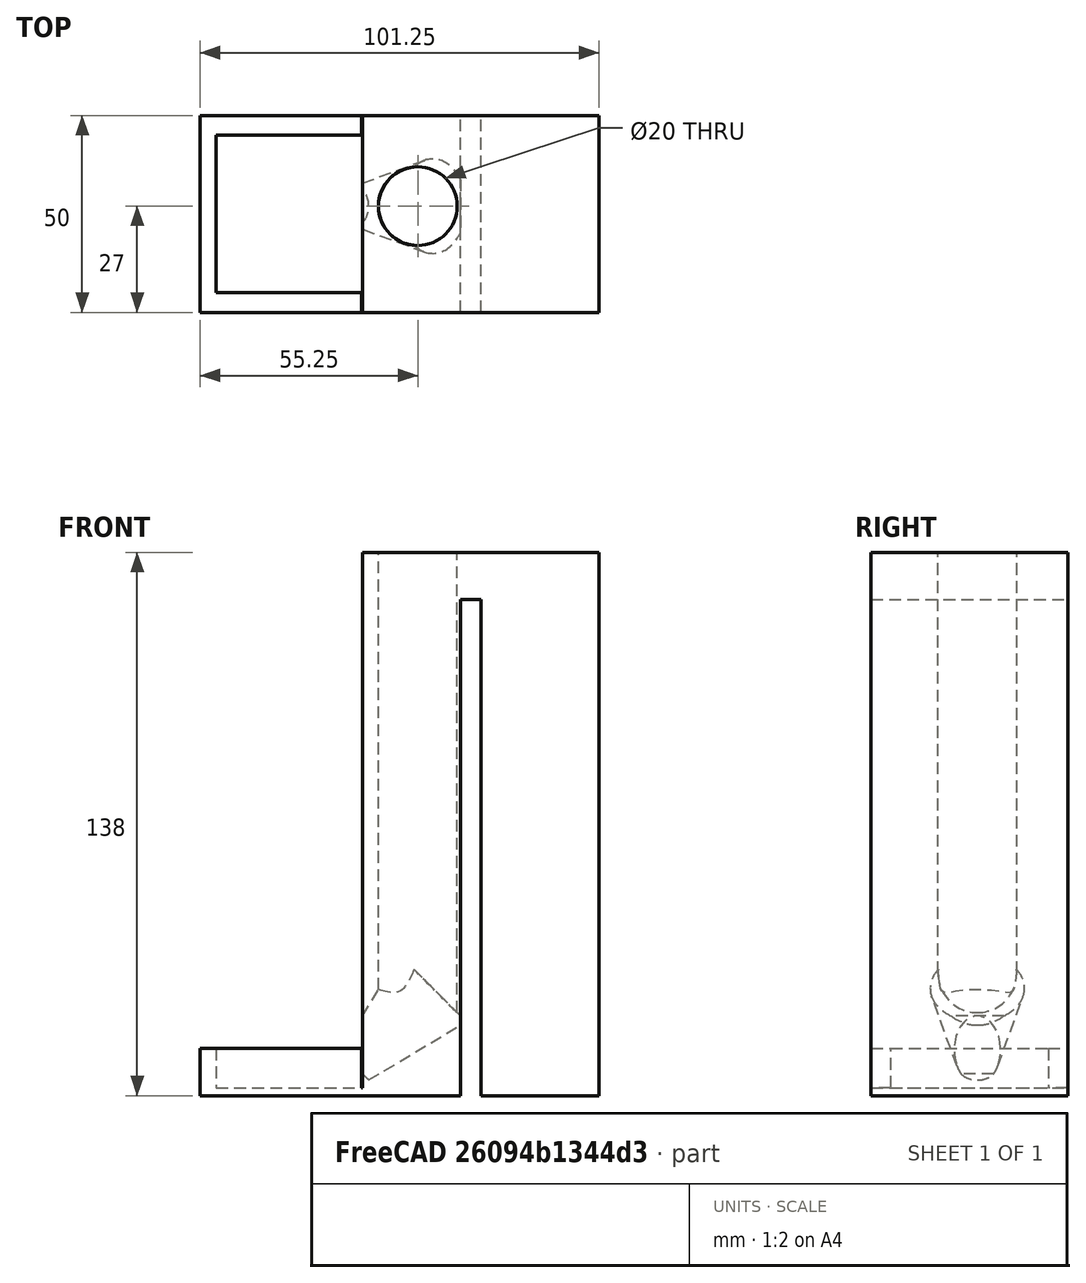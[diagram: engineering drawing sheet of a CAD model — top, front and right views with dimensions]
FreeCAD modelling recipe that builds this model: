
FCSTD DOCUMENT  (FreeCAD 0.17R13522 (Git))
Label: new reward no top
License: All rights reserved
LicenseURL: http://en.wikipedia.org/wiki/All_rights_reserved
objects: Part::Box×6, Part::Fuse×4, Part::Cut×3, Part::Cylinder×1, Part::Cone×1
note: 15 computed .brp shape members not serialized (recipe doc carries the construction recipe); baked Part::Feature solids carry a one-line shape summary decoded from their .brp

FEATURE [Part::Box] Box001  label="Cube001"
  AttacherType = Attacher::AttachEngine3D
  Height = 138
  Length = 60
  Placement = pos=(-30,32,-10) rot=(0,0,1;0rad)
  Width = 50
FEATURE [Part::Box] Box002  label="Cube002"
  AttacherType = Attacher::AttachEngine3D
  Height = 126
  Length = 5.2
  Placement = pos=(-5.2,32,-10) rot=(0,0,1;0rad)
  Width = 50
FEATURE [Part::Cylinder] Cylinder
  Angle = 360
  AttacherType = Attacher::AttachEngine3D
  Height = 129
  Placement = pos=(-16,59,11) rot=(0,0,1;0rad)
  Radius = 10
FEATURE [Part::Cone] Cone001
  Angle = 360
  AttacherType = Attacher::AttachEngine3D
  Height = 28
  Placement = pos=(-32,59,-2.5) rot=(0,1,0;0.785398rad)
  Radius1 = 5
  Radius2 = 12
FEATURE [Part::Box] Box007  label="Cube007"
  AttacherType = Attacher::AttachEngine3D
  Height = 12
  Length = 41
  Placement = pos=(-215,221,-4) rot=(0,0,1;0rad)
  Width = 5
FEATURE [Part::Box] Box006  label="Cube006"
  AttacherType = Attacher::AttachEngine3D
  Height = 12
  Length = 41
  Placement = pos=(-215,176,-4) rot=(0,0,1;0rad)
  Width = 5
FEATURE [Part::Box] Box004  label="Cube004"
  AttacherType = Attacher::AttachEngine3D
  Height = 2
  Length = 66
  Placement = pos=(-215,176,-4) rot=(0,0,1;0rad)
  Width = 50
FEATURE [Part::Box] Box005  label="Cube005"
  AttacherType = Attacher::AttachEngine3D
  Height = 12
  Length = 4
  Placement = pos=(-215,176,-4) rot=(0,0,1;0rad)
  Width = 50
FEATURE [Part::Fuse] Fusion
  Base = -> Box007
  Tool = -> Box006
FEATURE [Part::Fuse] Fusion001
  Base = -> Box004
  Tool = -> Box005
FEATURE [Part::Fuse] Fusion002
  Base = -> Fusion
  Placement = pos=(143.75,-144,-6) rot=(0,0,1;0rad)
  Tool = -> Fusion001
FEATURE [Part::Cut] Cut
  Base = -> Box001
  Tool = -> Box002
FEATURE [Part::Cut] Cut001
  Base = -> Cut
  Tool = -> Cone001
FEATURE [Part::Cut] Cut002
  Base = -> Cut001
  Tool = -> Cylinder
FEATURE [Part::Fuse] Fusion003
  Base = -> Fusion002
  Tool = -> Cut002
